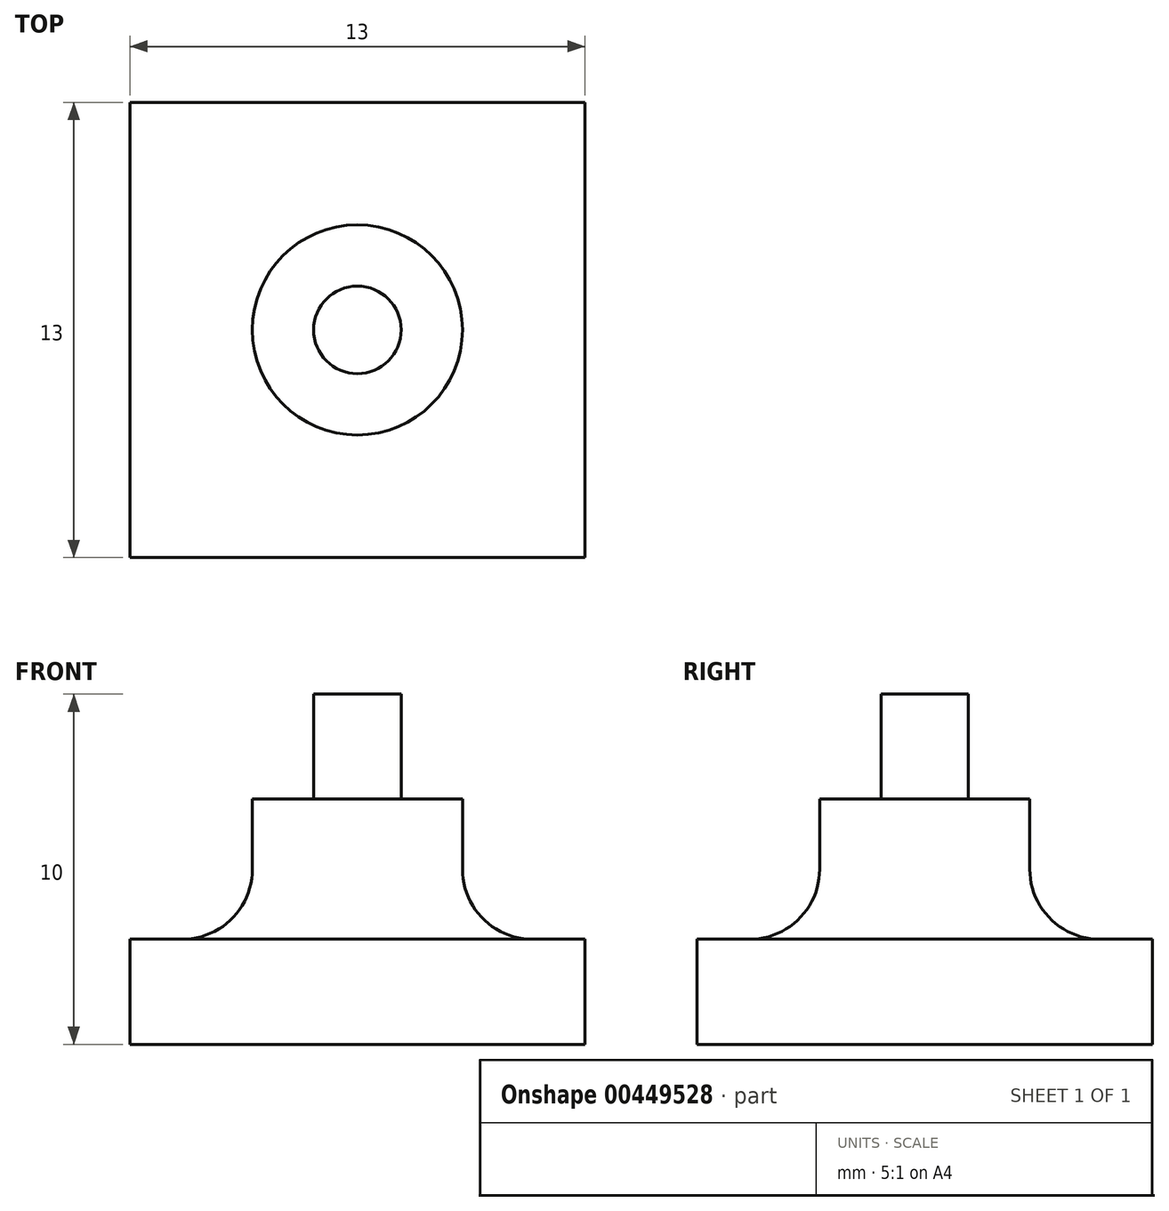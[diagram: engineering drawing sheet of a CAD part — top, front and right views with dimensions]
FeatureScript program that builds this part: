
annotation { "Feature Type Name" : "Feature", "Feature Type Description" : "" }
export const myFeature = defineFeature(function(context is Context, id is Id, definition is map)
    precondition{}
    {
        {
            var Q0;
            Q0=qCreatedBy(makeId("Top.planeOp"),FACE);
            var sketch = newSketch(context, id + "F0", { "sketchPlane" : qUnion([Q0])});
            skLineSegment(sketch, "E0.bottom", {"start": v(0, 0) * mm, "end": v(13, 0) * mm});
            skLineSegment(sketch, "E0.top", {"start": v(0, 13) * mm, "end": v(13, 13) * mm});
            skLineSegment(sketch, "E0.left", {"start": v(0, 0) * mm, "end": v(0, 13) * mm});
            skLineSegment(sketch, "E0.right", {"start": v(13, 0) * mm, "end": v(13, 13) * mm});
            skCircle(sketch, "E1", {"center": v(6.5, 6.5) * mm, "radius": 3 * mm});
            skCircle(sketch, "E2", {"center": v(6.5, 6.5) * mm, "radius": 1.25 * mm});
            skLineSegment(sketch, "E3", {"start": v(0, 13) * mm, "end": v(13, 0) * mm, "construction": true});
            skLineSegment(sketch, "E4", {"start": v(13, 13) * mm, "end": v(0, 0) * mm, "construction": true});
            skSolve(sketch);
        }
        {
            var Q0;
            Q0=makeQuery(id+"F0.imprint","IMPRINT",FACE,{"disambiguationData":[TD([[makeQuery(id+"F0.imprint","IMPRINT",EDGE,{"derivedFrom":sQuery(id+"F0.wireOp",EDGE,"E0.bottom")}),1.0]])]});
            var Q1;
            Q1=makeQuery(id+"F0.imprint","IMPRINT",FACE,{"disambiguationData":[TD([[makeQuery(id+"F0.imprint","IMPRINT",EDGE,{"derivedFrom":sQuery(id+"F0.wireOp",EDGE,"E1")}),1.0]])]});
            var Q2;
            Q2=makeQuery(id+"F0.imprint","IMPRINT",FACE,{"disambiguationData":[TD([[makeQuery(id+"F0.imprint","IMPRINT",EDGE,{"derivedFrom":sQuery(id+"F0.wireOp",EDGE,"E2")}),1.0]])]});
            extrude(context, id + "F1", {"entities" : qUnion([Q0, Q1, Q2]), "depth" : 3 * mm, "offsetDistance" : 25 * mm});
        }
        {
            var Q0;
            Q0=makeQuery(id+"F0.imprint","IMPRINT",FACE,{"disambiguationData":[TD([[makeQuery(id+"F0.imprint","IMPRINT",EDGE,{"derivedFrom":sQuery(id+"F0.wireOp",EDGE,"E1")}),1.0]])]});
            var Q1;
            Q1=makeQuery(id+"F0.imprint","IMPRINT",FACE,{"disambiguationData":[TD([[makeQuery(id+"F0.imprint","IMPRINT",EDGE,{"derivedFrom":sQuery(id+"F0.wireOp",EDGE,"E2")}),1.0]])]});
            extrude(context, id + "F2", {"entities" : qUnion([Q0, Q1]), "operationType" : NewBodyOperationType.ADD, "depth" : 7 * mm, "offsetDistance" : 25 * mm});
        }
        {
            var Q0;
            Q0=makeQuery(id+"F0.imprint","IMPRINT",FACE,{"disambiguationData":[TD([[makeQuery(id+"F0.imprint","IMPRINT",EDGE,{"derivedFrom":sQuery(id+"F0.wireOp",EDGE,"E2")}),1.0]])]});
            extrude(context, id + "F3", {"entities" : qUnion([Q0]), "operationType" : NewBodyOperationType.ADD, "depth" : 10 * mm, "offsetDistance" : 25 * mm});
        }
        {
            var Q0;
            Q0=makeQuery(id+"F2.boolean.opBoolean","INTERSECT",EDGE,{"derivedFrom":[makeQuery(id+"F1.opExtrude","CAP_FACE",FACE,{"disambiguationData":[OSD([sQuery(id+"F0.wireOp",EDGE,"E0.bottom"),sQuery(id+"F0.wireOp",EDGE,"E0.top"),sQuery(id+"F0.wireOp",EDGE,"E0.left"),sQuery(id+"F0.wireOp",EDGE,"E0.right")])],"isStart":false}),makeQuery(id+"F2.opExtrude","SWEPT_FACE",FACE,{"disambiguationData":[OSD([sQuery(id+"F0.wireOp",EDGE,"E1")])]})]});
            fillet(context, id + "F4", {"entities" : qUnion([Q0]), "radius" : 2 * mm, "tangentPropagation" : true, "allowEdgeOverflow" : false});
        }
    });
